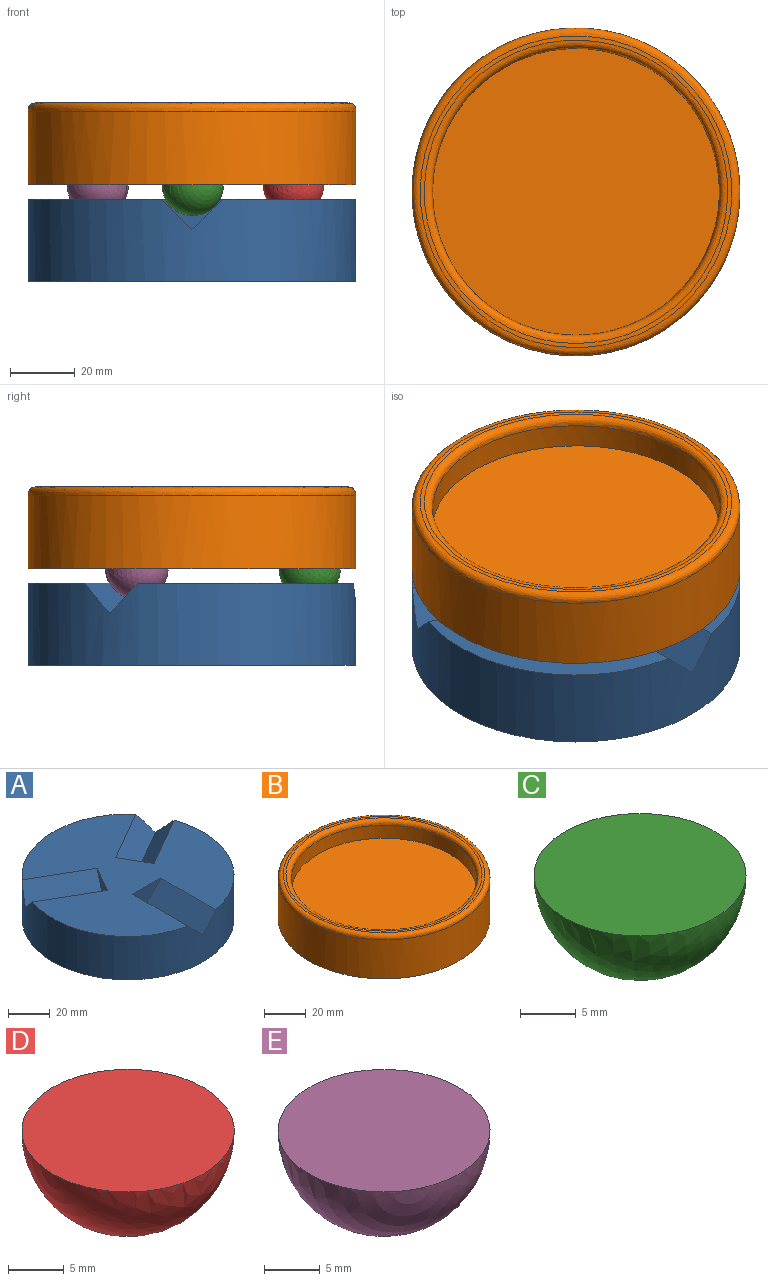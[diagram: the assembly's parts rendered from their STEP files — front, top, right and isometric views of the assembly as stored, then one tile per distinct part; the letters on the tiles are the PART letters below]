
ASSEMBLY  parts=5 mates=4
PART A: 12 faces, bbox 101.6x101.6x25.4 mm
  f0: plane 16.5x9.53mm, normal (0.87,0.5,0), area 90.7mm2, adj f4,f5,f11
  f1: plane 16.5x9.53mm, normal (-0.87,0.5,0), area 90.7mm2, adj f6,f7,f11
  f2: cylinder r=50.8mm len=101.6mm, axis (0,0,-1), area 7834.3mm2, adj f4,f5,f6,f7,f8,f9,f10,f11
  f3: plane 19.05x9.53mm, normal (0,-1,0), area 90.7mm2, adj f9,f10,f11
  f4: plane 37.76x26.85mm, normal (0.35,-0.61,0.71), area 509.2mm2, adj f0,f2,f5,f11
  f5: plane 36.98x27.3mm, normal (-0.35,0.61,0.71), area 509.2mm2, adj f0,f2,f4,f11
  f6: plane 36.98x27.3mm, normal (0.35,0.61,0.71), area 509.2mm2, adj f1,f2,f7,f11
  f7: plane 37.76x26.85mm, normal (-0.35,-0.61,0.71), area 509.2mm2, adj f1,f2,f6,f11
  f8: plane 101.6x101.6mm, normal (0,0,-1), area 8107.3mm2, adj f2
  f9: plane 38.1x9.53mm, normal (-0.71,0,0.71), area 509.2mm2, adj f2,f3,f10,f11
  f10: plane 38.1x9.53mm, normal (0.71,0,0.71), area 509.2mm2, adj f2,f3,f9,f11
  f11: plane 101.6x100.7mm, normal (0,0,1), area 5947mm2, adj f0,f1,f2,f3,f4,f5,f6,f7
PART B: 7 faces, bbox 104.3x104.3x25.4 mm
  f0: cylinder r=50.8mm len=101.6mm, axis (0,0,-1), area 7296.6mm2, adj f2,f6
  f1: plane 96.54x96.54mm, normal (0,0,1), area 380mm2, adj f5,f6
  f2: plane 101.6x101.6mm, normal (0,0,-1), area 8107.3mm2, adj f0
  f3: cylinder r=44.45mm len=88.9mm, axis (0,0,1), area 2128.2mm2, adj f4,f5
  f4: plane 88.9x88.9mm, normal (0,0,1), area 6207.2mm2, adj f3
  f5: bspline ~96.43x96.43mm, area 1176mm2, adj f1,f3
  f6: bspline ~104.25x104.25mm, area 1295.9mm2, adj f0,f1
PART C: 2 faces, bbox 19.1x19.1x9.5 mm
  f0: sphere r=9.53mm, area 570mm2, adj f1
  f1: plane 19.05x19.05mm, normal (0,0,1), area 285mm2, adj f0
PART D: 2 faces, bbox 19.1x19.1x9.5 mm
  f0: sphere r=9.53mm, area 570mm2, adj f1
  f1: plane 19.05x19.05mm, normal (0,0,1), area 285mm2, adj f0
PART E: 2 faces, bbox 19.1x19.1x9.5 mm
  f0: sphere r=9.53mm, area 570mm2, adj f1
  f1: plane 19.05x19.05mm, normal (0,0,1), area 285mm2, adj f0
PLACE A t=(-38.37,88.6,-63.76)mm
PLACE B t=(-38.37,88.6,-59.35)mm
PLACE C t=(-57.2,85.11,-59.35)mm
PLACE D t=(31.17,105.89,-59.35)mm
PLACE E t=(-86.65,72.53,-59.35)mm
MATE cylindrical B.f0 <-> A.f2  axis (0,0,-1) through (-38.37,88.6,-47.92)mm
MATE planar C.f1 <-> B.f0  axis (0,0,1) through (-38.15,52.12,-59.35)mm
MATE planar B.f0 <-> E.f1  axis (0,0,-1) through (-38.37,88.6,-59.35)mm
MATE planar D.f1 <-> B.f0  axis (0,0,1) through (-6.93,105.89,-59.35)mm
